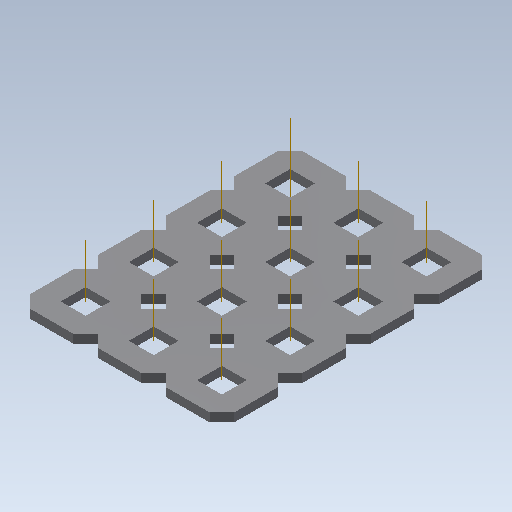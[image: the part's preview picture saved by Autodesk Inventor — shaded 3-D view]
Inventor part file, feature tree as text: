
AUTODESK INVENTOR PART (.ipt)
format: ipt  version: 2020 (Build 240168000, 168)  size: 1,125,888 bytes
history: native  units: in
note: dims shown in document units (in); Inventor stores cm internally (conversion verified against a paired STEP export)
features: other x21, extrude x2, pattern_linear x1, imported_body x1
ambient origin geometry x8: Origin, YZ Plane, XZ Plane, XY Plane, X Axis, Y Axis, Z Axis, Center Point
bodies: Body1 (feature_tree)
feature tree (25):
  other  "Diamond-Pattern"
  other  "Plate"
  extrude  "length cut"  TaperAngle=0.0deg  [1 undecoded]
  extrude  "width cut"  TaperAngle=0.0deg  [1 undecoded]
  other  "constraint axis"
  pattern_linear  "constraint axes"  Spacing1=0.5in  [1 undecoded]
  other  "front plane"
  other  "right plane"
  imported_body  "Base1"
  other  "length profile"
  other  "width profile"
  other  "Work Point1"
  other  "Work Axis36"
  other  "Work Axis37"
  other  "Work Axis38"
  other  "Work Axis40"
  other  "Work Axis41"
  other  "Work Axis42"
  other  "Work Axis43"
  other  "Work Axis44"
  other  "Work Axis45"
  other  "Work Axis46"
  other  "Work Axis47"
  other  "back plane"
  other  "left plane"
note: 3 required parameter values undecoded (feature->parameter linkage not recoverable at this tier; creation-order binding heuristic only, values carry confidence <= 0.55)
